# Revit family: 0049128 Feilo Sylvania Lighting Fixture SYLVEO LED 30000LM WIDE 3K
name_source: partatom
category: Lighting Fixtures
revit_build: Autodesk Revit 2017 (Build: 20190507_1515(x64)
units: mm (PartAtom-declared; Revit-internal decimal feet)

## family parameters
Cut with Voids When Loaded = No
Host = Face
Light Source = No
OmniClass Number = 23.80.70.00
OmniClass Title = Lighting
Part Type = Normal
Room Calculation Point = No
Round Connector Dimension = Use Diameter
Shared = Yes

## types (1)
- 0049128 SYLVEO LED 30000LM WIDE 3K
    Apparent Load = 301 VA
    Assembly Code = D5020200
    AssetType = Fixed
    BracketExtrusionEnd_FEILO = 24 mm  [stored 0.0787402 ft]
    BracketExtrusionStart_FEILO = -24 mm  [stored -0.0787402 ft]
    BracketFold_FEILO = 30 mm  [stored 0.0984252 ft]
    BracketInnerWidth_FEILO = 623 mm  [stored 2.04396 ft]
    BracketThickness_FEILO = 5 mm  [stored 0.0164042 ft]
    BracketWidth_FEILO = 48 mm  [stored 0.15748 ft]
    ClassificationName = Uniclass2015
    ClassificationValue = EF_70_80
    Cost = 0 $
    Default Elevation = 1219 mm
    Description = Exterior LED Floodlight, comes complete with a 1000mm cable and adjustable bracket, aluminium housing, clear glass diffuser, IP66, IK08, Class I, 3000K, Non-dimming, 30813lm, 301W, 102lm/W, 8400mA, CRI70, 52° beam angle, 50000hrs, (LxWxD) 98x648x392mm
    DimmingControlOptions = Non dimmable
    DocumentationLiterature = http://www.sylvania-lighting.com
    DurationUnit = hours
    ElectricShockClassification = Class I
    ExpectedLife = 50000
    HingeDia_FEILO = 70 mm  [stored 0.229659 ft]
    HingeHeight_FEILO = 121 mm  [stored 0.396982 ft]
    IfcExportAs = IfcLightFixtureType
    IfcExportType = IfcLightFixtureType
    ImpactProtectionIndex = IK08
    IngressProtection = IP66
    InputNominalFrequency = 50 Hz
    InputVoltage = 100-240V~
    Keynote = 16500
    Lamp = LED
    LampColourRenderingIndex = 70
    LampColourTemperature = 3000 K
    LampMacAdamStep = 6
    LampNominalLuminous = 30813 lm
    LampsType = LED
    LightOutputRatio = 100
    LuminousEfficacy = 102.3 lm/W
    Manufacturer = Feilo Sylvania
    ManufacturerName = Feilo Sylvania
    Material = aluminium housing, glass diffuser
    Material_1_FEILO = Body-Sylvania-Sylveo-Aluminium
    Material_2_FEILO = <By Category>
    Material_3_FEILO = <By Category>
    Material_4_FEILO = <By Category>
    Model = SYLVEO LED 30000LM WIDE 3K
    ModelNumber = 0049128
    ModelReference = SYLVEO LED 30000LM WIDE 3K
    Name = SYLVEO LED 30000LM WIDE 3K
    NominalHeight = 392 mm  [stored 1.28609 ft]
    NominalLength = 648 mm  [stored 2.12598 ft]
    NominalWidth = 0 mm  [stored 0 ft]
    PowerConsumption = 301.2 W
    PowerFactor = 0
    TotalWidth_FEILO = 648 mm  [stored 2.12598 ft]
    Type Image = <None>
    TypeBody_FEILO = Sylveo Extra Large Body : 0049128 SYLVEO LED 30000LM WIDE 3K
    TypeName = SYLVEO LED 30000LM WIDE 3K
    URL = http://www.sylvania-lighting.com
    Voltage = 230 V
    Weight = 15.868 kg

note: [stored X ft] marks values corroborated as IEEE doubles in the binary element streams (Revit-internal decimal feet)

## geometry (parser evidence)
native form markers: Extrusion x2, Sweep x10
no freeform markers — native parametric forms only
